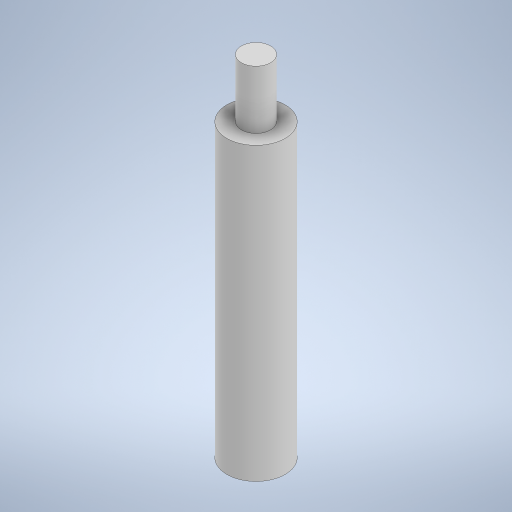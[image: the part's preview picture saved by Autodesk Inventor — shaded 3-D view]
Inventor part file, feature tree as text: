
AUTODESK INVENTOR PART (.ipt)
format: ipt  version: 2023 (Build 270158030, 158C)  size: 234,496 bytes
history: native  units: mm
features: extrude x2, sketch x2
ambient origin geometry x8: Origin, YZ Plane, XZ Plane, XY Plane, X Axis, Y Axis, Z Axis, Center Point
bodies: Solid1 (feature_tree)
feature tree (4):
  extrude  "Extrusion1"  Depth=50.0mm TaperAngle=0.0deg
  extrude  "Extrusion2"  Depth=10.0mm TaperAngle=0.0deg
  sketch  "Sketch1"  dims[d0=10.0mm d1=50.0mm d2=0.0mm]
  sketch  "Sketch2"  dims[d3=5.0mm d4=10.0mm d5=0.0mm]
